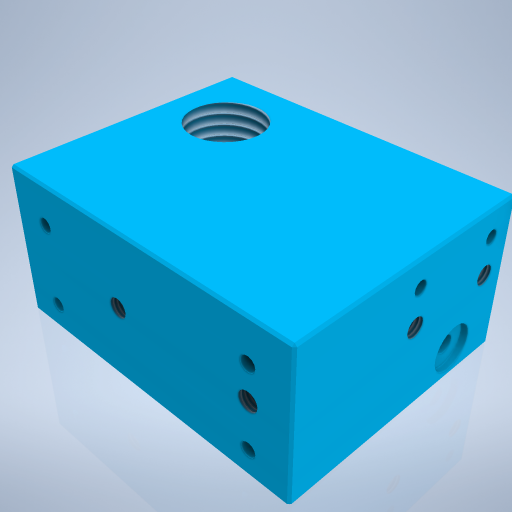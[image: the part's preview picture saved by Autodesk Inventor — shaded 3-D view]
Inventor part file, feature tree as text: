
AUTODESK INVENTOR PART (.ipt)
format: ipt  version: 2024.2 (Build 282272000, 272)  size: 316,416 bytes
history: native  units: mm
features: hole x7, sketch x7, chamfer x2, extrude x1, plane x1, mirror x1
ambient origin geometry x8: Origin, YZ Plane, XZ Plane, XY Plane, X Axis, Y Axis, Z Axis, Center Point
bodies: Volumenkörper1 (feature_tree)
feature tree (19):
  extrude  "Extrusion1"  Depth=55.0mm
  hole  "Bohrung1"  [1 undecoded]
  sketch  "Skizze4"  dims[d4=17.294mm d5=18.0mm d6=4.0mm d7=2.0mm d8=90.0deg d9=23.0mm d10=20.594885mm d11=15.0mm]
  hole  "Bohrung3"  [1 undecoded]
  hole  "Bohrung4"  [1 undecoded]
  hole  "Bohrung5"  [1 undecoded]
  hole  "Bohrung6"  [1 undecoded]
  hole  "Bohrung7"  [1 undecoded]
  plane  "Arbeitsebene1"
  mirror  "Spiegeln1"
  hole  "Bohrung8"  [1 undecoded]
  chamfer  "Fasen1"  Distance=9.0mm
  chamfer  "Fasen2"  Distance=9.0mm
  sketch  "Skizze1"  dims[d0=69.5mm d1=55.0mm]
  sketch  "Skizze2"  dims[d2=33.0mm d3=0.0mm]
  sketch  "Skizze5"  dims[d12=39.0mm d21=29.0mm]
  sketch  "Skizze6"  dims[d22=20.0mm d23=27.0mm]
  sketch  "Skizze7"  dims[d24=27.0mm]
  sketch  "Skizze8"  dims[d27=4.134mm d28=11.0mm d29=4.0mm d30=2.0mm d31=90.0deg d32=15.0mm d33=20.594885mm d34=3.0mm d35=11.0mm d36=4.0mm d37=2.0mm d38=90.0deg d39=8.0mm d40=20.594885mm d41=4.0mm d42=6.0mm d43=10.0mm d44=1.5mm d45=90.0deg d46=50.0mm d47=0.0mm d48=6.5mm d49=13.0mm d50=3.2mm d51=6.0mm d52=10.0mm d53=1.5mm d54=90.0deg d55=8.0mm d56=20.594885mm d57=6.0mm d58=18.0mm d59=9.0mm d60=9.0mm d61=4.134mm d62=13.0mm d63=4.0mm d64=2.0mm d65=90.0deg d66=17.0mm d67=20.594885mm d68=0.0mm d69=4.134mm d70=13.0mm d71=4.0mm d72=2.0mm d73=90.0deg d74=17.0mm d75=20.594885mm d76=29.0mm d77=16.5mm d78=0.5mm d79=2.0mm d80=45.0deg d81=0.5mm d82=2.0mm d83=45.0deg d85=8.0mm]
note: 7 required parameter values undecoded (feature->parameter linkage not recoverable at this tier; creation-order binding heuristic only, values carry confidence <= 0.55)
